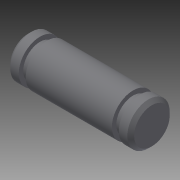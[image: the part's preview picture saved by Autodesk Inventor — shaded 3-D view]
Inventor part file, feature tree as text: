
AUTODESK INVENTOR PART (.ipt)
format: ipt  version: 2014 (Build 180170000, 170)  size: 126,464 bytes
history: native  units: in
note: dims shown in document units (in); Inventor stores cm internally (conversion verified against a paired STEP export)
features: other x49, revolve x1, sketch x1
ambient origin geometry x8: Origin, YZ Plane, XZ Plane, XY Plane, X Axis, Y Axis, Z Axis, Center Point
bodies: Solid1 (feature_tree)
feature tree (51):
  revolve  "Revolution1"  [1 undecoded]
  other  "p1_XY"
  other  "p1_YZ"
  other  "p1_ZX"
  other  "p1_X"
  other  "p1_Y"
  other  "p1_Z"
  other  "p1_Center"
  other  "p2_XY"
  other  "p2_YZ"
  other  "p2_ZX"
  other  "p2_X"
  other  "p2_Y"
  other  "p2_Z"
  other  "p2_Center"
  other  "pin_XY"
  other  "pin_YZ"
  other  "pin_ZX"
  other  "pin_X"
  other  "pin_Y"
  other  "pin_Z"
  other  "pin_Center"
  other  "rr1_XY"
  other  "rr1_YZ"
  other  "rr1_ZX"
  other  "rr1_X"
  other  "rr1_Y"
  other  "rr1_Z"
  other  "rr1_Center"
  other  "rr2_XY"
  other  "rr2_YZ"
  other  "rr2_ZX"
  other  "rr2_X"
  other  "rr2_Y"
  other  "rr2_Z"
  other  "rr2_Center"
  other  "w21_XY"
  other  "w21_YZ"
  other  "w21_ZX"
  other  "w21_X"
  other  "w21_Y"
  other  "w21_Z"
  other  "w21_Center"
  other  "w22_XY"
  other  "w22_YZ"
  other  "w22_ZX"
  other  "w22_X"
  other  "w22_Y"
  other  "w22_Z"
  other  "w22_Center"
  sketch  "Sketch_1"  dims[d0=360.0deg]
note: 1 required parameter value undecoded (feature->parameter linkage not recoverable at this tier; creation-order binding heuristic only, values carry confidence <= 0.55)
